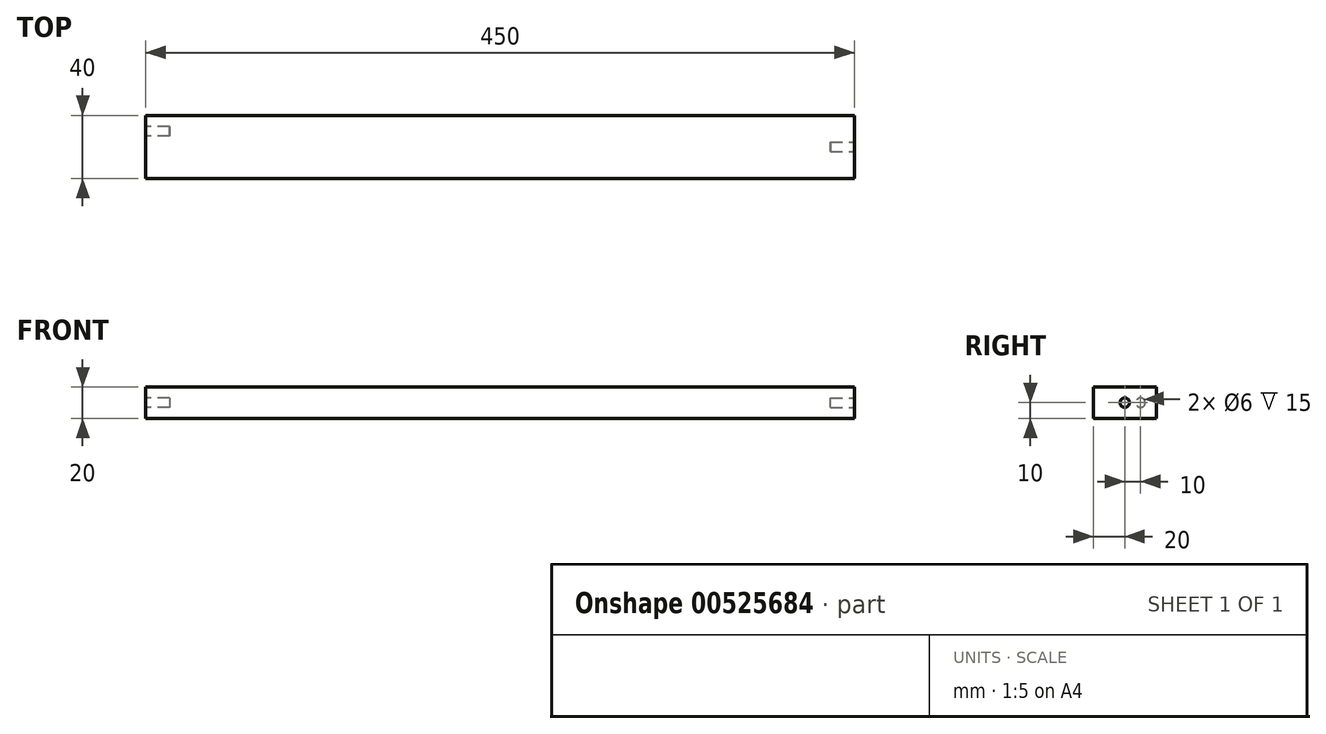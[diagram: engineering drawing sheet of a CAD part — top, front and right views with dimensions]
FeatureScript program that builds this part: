
annotation { "Feature Type Name" : "Feature", "Feature Type Description" : "" }
export const myFeature = defineFeature(function(context is Context, id is Id, definition is map)
    precondition{}
    {
        {
            var Q0;
            Q0=qCreatedBy(makeId("Right.planeOp"),FACE);
            var sketch = newSketch(context, id + "F0", { "sketchPlane" : qUnion([Q0])});
            skLineSegment(sketch, "E0.bottom", {"start": v(0, 0) * mm, "end": v(40, 0) * mm});
            skLineSegment(sketch, "E0.top", {"start": v(0, 20) * mm, "end": v(40, 20) * mm});
            skLineSegment(sketch, "E0.left", {"start": v(0, 0) * mm, "end": v(0, 20) * mm});
            skLineSegment(sketch, "E0.right", {"start": v(40, 0) * mm, "end": v(40, 20) * mm});
            skSolve(sketch);
        }
        {
            var Q0;
            Q0=makeQuery(id+"F0.imprint","IMPRINT",FACE,{"disambiguationData":[TD([[makeQuery(id+"F0.imprint","IMPRINT",EDGE,{"derivedFrom":sQuery(id+"F0.wireOp",EDGE,"E0.bottom")}),1.0]])]});
            extrude(context, id + "F1", {"entities" : qUnion([Q0]), "depth" : 450 * mm, "offsetDistance" : 25 * mm});
        }
        {
            var Q0;
            Q0=makeQuery(id+"F1.opExtrude","CAP_FACE",FACE,{"disambiguationData":[OSD([sQuery(id+"F0.wireOp",EDGE,"E0.bottom"),sQuery(id+"F0.wireOp",EDGE,"E0.top"),sQuery(id+"F0.wireOp",EDGE,"E0.left"),sQuery(id+"F0.wireOp",EDGE,"E0.right")])],"isStart":false});
            var sketch = newSketch(context, id + "F2", { "sketchPlane" : qUnion([Q0])});
            skCircle(sketch, "E1", {"center": v(20, 10) * mm, "radius": 3 * mm});
            skSolve(sketch);
        }
        {
            var Q0;
            Q0=makeQuery(id+"F2.imprint","IMPRINT",FACE,{"disambiguationData":[TD([[makeQuery(id+"F2.imprint","IMPRINT",EDGE,{"derivedFrom":sQuery(id+"F2.wireOp",EDGE,"E1")}),1.0]])]});
            extrude(context, id + "F3", {"entities" : qUnion([Q0]), "operationType" : NewBodyOperationType.REMOVE, "oppositeDirection" : true, "depth" : 15 * mm, "offsetDistance" : 25 * mm});
        }
        {
            var Q0;
            Q0=makeQuery(id+"F1.opExtrude","CAP_FACE",FACE,{"disambiguationData":[OSD([sQuery(id+"F0.wireOp",EDGE,"E0.bottom"),sQuery(id+"F0.wireOp",EDGE,"E0.top"),sQuery(id+"F0.wireOp",EDGE,"E0.left"),sQuery(id+"F0.wireOp",EDGE,"E0.right")])],"isStart":true});
            var sketch = newSketch(context, id + "F4", { "sketchPlane" : qUnion([Q0])});
            skCircle(sketch, "E2", {"center": v(-30, 10) * mm, "radius": 3 * mm});
            skSolve(sketch);
        }
        {
            var Q0;
            Q0=makeQuery(id+"F4.imprint","IMPRINT",FACE,{"disambiguationData":[TD([[makeQuery(id+"F4.imprint","IMPRINT",EDGE,{"derivedFrom":sQuery(id+"F4.wireOp",EDGE,"E2")}),1.0]])]});
            extrude(context, id + "F5", {"entities" : qUnion([Q0]), "operationType" : NewBodyOperationType.REMOVE, "oppositeDirection" : true, "depth" : 15 * mm, "offsetDistance" : 25 * mm});
        }
    });
